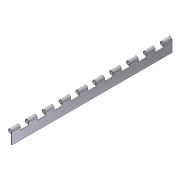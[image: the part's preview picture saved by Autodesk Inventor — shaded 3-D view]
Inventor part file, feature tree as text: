
AUTODESK INVENTOR PART (.ipt)
format: ipt  version: 2012 (Build 160160000, 160)  size: 146,944 bytes
history: native  units: in
note: dims shown in document units (in); Inventor stores cm internally (conversion verified against a paired STEP export)
features: extrude x2, sketch x2, fillet x1, pattern_linear x1, projected_geometry x1
ambient origin geometry x8: Origin, YZ Plane, XZ Plane, XY Plane, X Axis, Y Axis, Z Axis, Center Point
bodies: Solid1 (feature_tree)
feature tree (7):
  extrude  "Extrusion1"  Depth=0.09in
  extrude  "Extrusion2"  Depth=19.0in TaperAngle=0.0deg
  fillet  "Fillet1"  Radius=1.0in
  pattern_linear  "Rectangular Pattern1"  Spacing1=1.0in  [1 undecoded]
  sketch  "Sketch1"  dims[d0=0.445in d1=0.09in]
  sketch  "Sketch2"  dims[d2=0.09in d3=19.0in d4=0.0in d5=1.0in d6=1.0in d7=0.125in d8=16.0in d9=0.0in d10=0.125in d11=3.5433in d13=2.0in]
  projected_geometry  "Projected Loop1"
note: 1 required parameter value undecoded (feature->parameter linkage not recoverable at this tier; creation-order binding heuristic only, values carry confidence <= 0.55)
